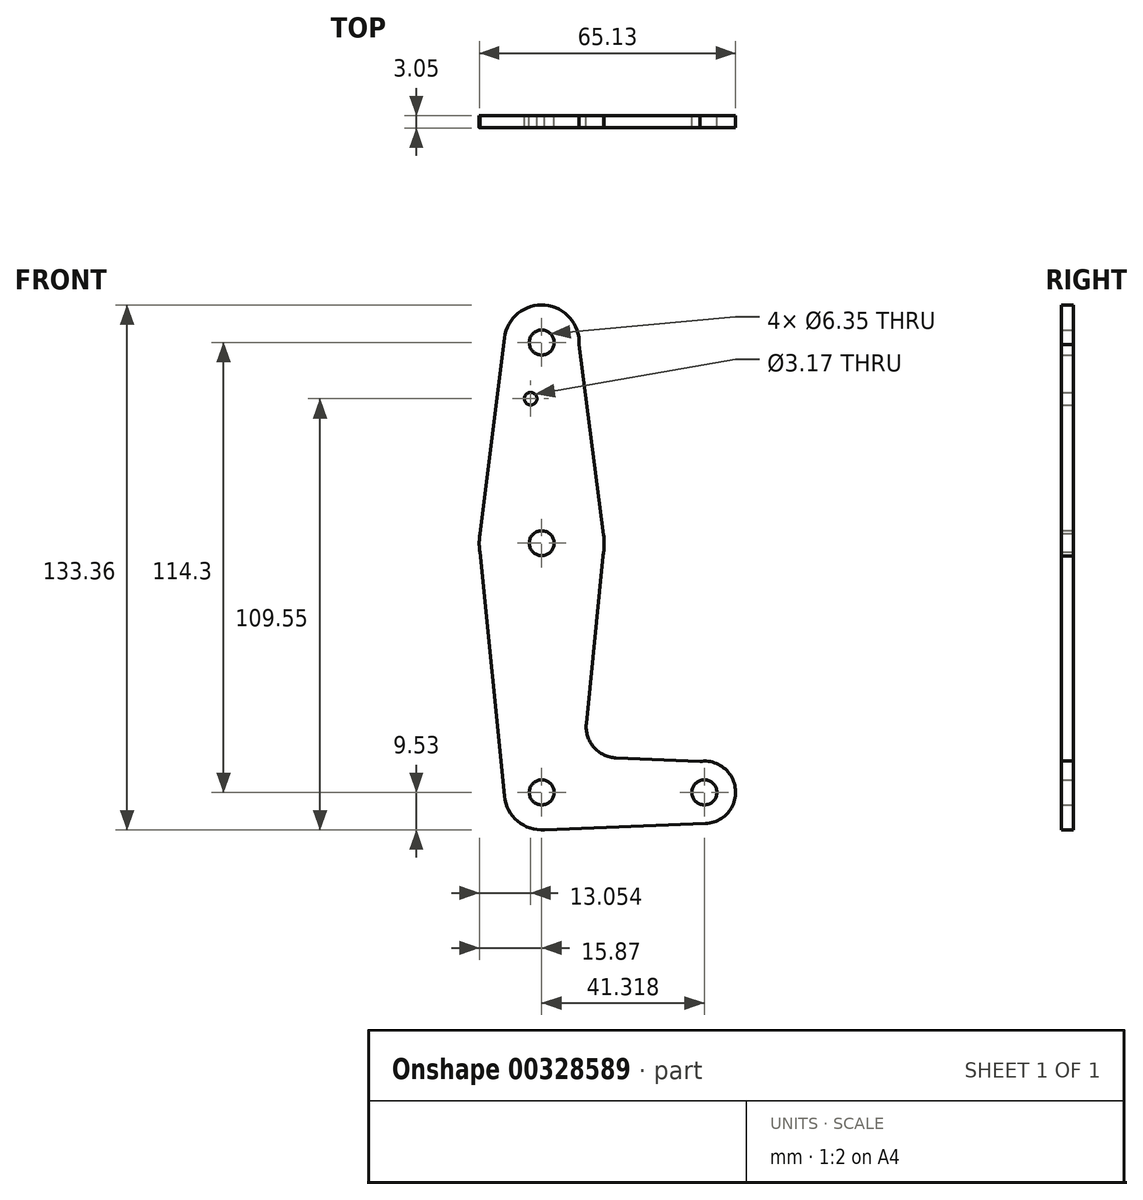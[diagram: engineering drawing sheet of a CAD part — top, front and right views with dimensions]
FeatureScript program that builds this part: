
annotation { "Feature Type Name" : "Feature", "Feature Type Description" : "" }
export const myFeature = defineFeature(function(context is Context, id is Id, definition is map)
    precondition{}
    {
        {
            var Q0;
            Q0=qCreatedBy(makeId("Front.planeOp"),FACE);
            var sketch = newSketch(context, id + "F0", { "sketchPlane" : qUnion([Q0])});
            skLineSegment(sketch, "E0", {"start": v(0, 0) * mm, "end": v(0, 114.3) * mm});
            skCircle(sketch, "E1", {"center": v(41.32, 0) * mm, "radius": 7.94 * mm});
            skCircle(sketch, "E2", {"center": v(0, 0) * mm, "radius": 9.53 * mm});
            skCircle(sketch, "E3", {"center": v(0, 63.3) * mm, "radius": 15.88 * mm});
            skCircle(sketch, "E4", {"center": v(0, 114.3) * mm, "radius": 9.53 * mm});
            skLineSegment(sketch, "E5", {"start": v(-15.69, 65.75) * mm, "end": v(-9.45, 115.48) * mm});
            skLineSegment(sketch, "E6", {"start": v(-15.72, 61.11) * mm, "end": v(-9.48, -0.95) * mm});
            skLineSegment(sketch, "E7", {"start": v(9.51, 113.82) * mm, "end": v(15.75, 65.33) * mm});
            skLineSegment(sketch, "E8", {"start": v(0, -9.53) * mm, "end": v(41.62, -7.93) * mm});
            skCircle(sketch, "E9", {"center": v(0, 114.3) * mm, "radius": 3.18 * mm});
            skCircle(sketch, "E10", {"center": v(0, 63.3) * mm, "radius": 3.18 * mm});
            skCircle(sketch, "E11", {"center": v(0, 0) * mm, "radius": 3.18 * mm});
            skCircle(sketch, "E12", {"center": v(41.32, 0) * mm, "radius": 3.18 * mm});
            skLineSegment(sketch, "E13", {"start": v(15.87, 63.46) * mm, "end": v(11.3, 17.47) * mm});
            skLineSegment(sketch, "E14", {"start": v(18.89, 8.74) * mm, "end": v(40.16, 7.85) * mm});
            skCircle(sketch, "E15", {"center": v(-2.82, 100.02) * mm, "radius": 1.59 * mm});
            skPoint(sketch, "E16.newPointA", {"position": v(0, 9.53) * mm});
            skPoint(sketch, "E16.newPointB", {"position": v(9.57, 0) * mm});
            skArc(sketch, "E16.filletArc", {"start": v(11.3, 17.47) * mm, "mid": v(13.22, 11.47) * mm, "end": v(18.89, 8.74) * mm});
            skSolve(sketch);
        }
        {
            var Q0;
            Q0 = qSketchRegion(id + "F0", true);
            extrude(context, id + "F1", {"entities" : qUnion([Q0]), "depth" : 3.05 * mm});
        }
        {
            var Q0;
            Q0 = qSketchRegion(id + "F0", true);
            extrude(context, id + "F2", {"entities" : qUnion([Q0]), "operationType" : NewBodyOperationType.ADD, "depth" : 3.05 * mm});
        }
    });
